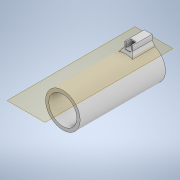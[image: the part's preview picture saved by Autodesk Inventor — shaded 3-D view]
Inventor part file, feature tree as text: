
AUTODESK INVENTOR PART (.ipt)
format: ipt  version: 2021 (Build 250183000, 183)  size: 466,944 bytes
history: native  units: in
note: dims shown in document units (in); Inventor stores cm internally (conversion verified against a paired STEP export)
features: projected_geometry x11, extrude x9, sketch x8, chamfer x4, plane x1, pattern_linear x1
ambient origin geometry x8: Origin, YZ Plane, XZ Plane, XY Plane, X Axis, Y Axis, Z Axis, Center Point
bodies: Solid1 (feature_tree)
feature tree (34):
  extrude  "Extrusion1"  Depth=4.3307in TaperAngle=0.0deg
  plane  "Work Plane1"
  extrude  "Extrusion7"  Depth=4.252in TaperAngle=0.0deg
  extrude  "Extrusion8"  Depth=0.9843in
  extrude  "Extrusion9"  Depth=0.2047in
  extrude  "Extrusion10"  Depth=0.1181in
  extrude  "Extrusion11"  Depth=0.0591in
  extrude  "Extrusion12"  Depth=0.0591in
  pattern_linear  "Rectangular Pattern3"  Spacing1=1.6142in  [1 undecoded]
  extrude  "Extrusion13"  Depth=1.811in
  chamfer  "Chamfer2"  Distance=0.0394in
  chamfer  "Chamfer4"  Distance=0.0098in
  chamfer  "Chamfer5"  Distance=8.2677in
  extrude  "Extrusion14"  Depth=0.248in
  chamfer  "Chamfer6"  Distance=0.3937in
  sketch  "Sketch2"  dims[d2=1.752in d3=4.3307in d4=0.0in]
  sketch  "Sketch9"  dims[d54=1.4173in d55=4.252in d56=0.0in]
  projected_geometry  "Projected Loop7"
  sketch  "Sketch10"  dims[d57=0.3937in d58=0.9843in]
  projected_geometry  "Projected Loop8"
  sketch  "Sketch11"  dims[d59=0.3937in d60=0.0236in d61=0.0in d62=0.0in d63=0.2047in]
  projected_geometry  "Projected Loop9"
  sketch  "Sketch12"  dims[d64=0.126in d65=0.1181in]
  projected_geometry  "Projected Loop10"
  projected_geometry  "Projected Loop11"
  projected_geometry  "Projected Loop12"
  sketch  "Sketch14"  dims[d66=0.0551in d67=0.0in d68=0.0591in]
  projected_geometry  "Projected Loop14"
  projected_geometry  "Projected Loop15"
  sketch  "Sketch16"  dims[d69=0.0591in d70=0.0591in]
  projected_geometry  "Projected Loop16"
  sketch  "Sketch17"  dims[d71=0.9646in d72=0.0in d76=1.6142in d77=0.0in d84=1.811in d85=0.0394in d86=0.0098in d87=0.0in d88=8.2677in d90=0.0787in d92=0.248in d93=0.3937in d94=0.0in d95=0.0787in d96=0.0059in d97=0.0185in d98=0.0787in d99=45.0deg d103=0.1575in d104=0.0787in d105=45.0deg d106=0.0098in d107=0.0787in d108=45.0deg d109=0.5906in d110=0.0315in d111=0.0in d112=0.0315in d113=0.0787in d114=45.0deg d19=0.0197in d20=0.0344in d21=0.0197in d22=0.0344in]
  projected_geometry  "Projected Loop17"
  projected_geometry  "Projected Loop18"
note: 1 required parameter value undecoded (feature->parameter linkage not recoverable at this tier; creation-order binding heuristic only, values carry confidence <= 0.55)
